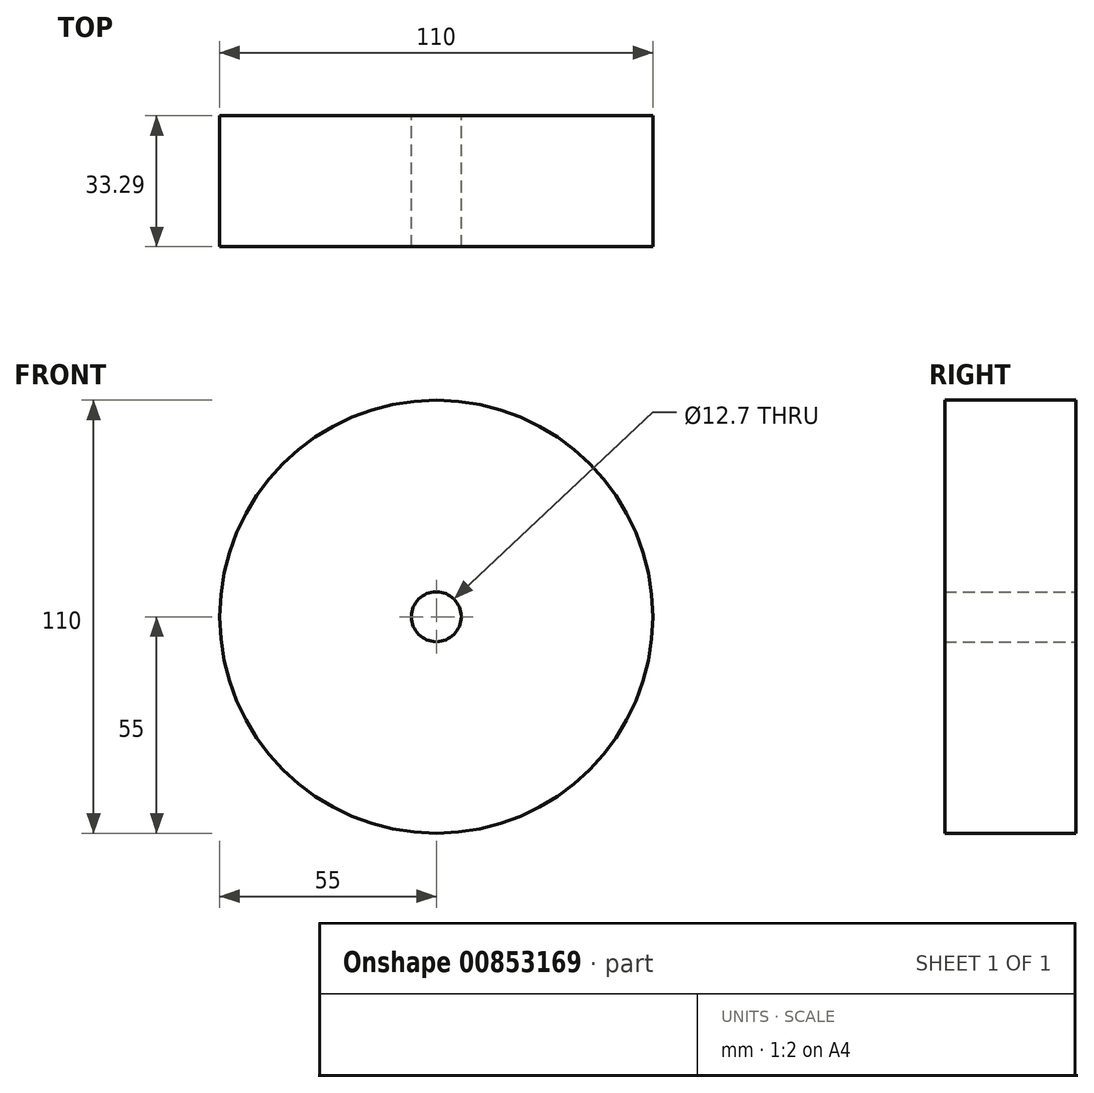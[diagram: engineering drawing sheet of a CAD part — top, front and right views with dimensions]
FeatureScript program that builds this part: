
annotation { "Feature Type Name" : "Feature", "Feature Type Description" : "" }
export const myFeature = defineFeature(function(context is Context, id is Id, definition is map)
    precondition{}
    {
        {
            var Q0;
            Q0=qCreatedBy(makeId("Front.planeOp"),FACE);
            var sketch = newSketch(context, id + "F0", { "sketchPlane" : qUnion([Q0])});
            skCircle(sketch, "E0", {"center": v(0, 0) * mm, "radius": 55 * mm});
            skSolve(sketch);
        }
        {
            var Q0;
            Q0=makeQuery(id+"F0.imprint","IMPRINT",FACE,{"disambiguationData":[TD([[makeQuery(id+"F0.imprint","IMPRINT",EDGE,{"derivedFrom":sQuery(id+"F0.wireOp",EDGE,"E0")}),1.0]])]});
            extrude(context, id + "F1", {"entities" : qUnion([Q0]), "depth" : 33.3 * mm, "offsetDistance" : 25.4 * mm});
        }
        {
            var Q0;
            Q0=qCreatedBy(makeId("Front.planeOp"),FACE);
            var sketch = newSketch(context, id + "F2", { "sketchPlane" : qUnion([Q0])});
            skPoint(sketch, "E1", {"position": v(0, 0) * mm});
            skSolve(sketch);
        }
        {
            var Q0;
            Q0=sQuery(id+"F2.wireOp",VERTEX,"E1");
            var Q1;
            Q1=makeQuery(id+"F1.opExtrude","SWEPT_BODY",BODY,{"disambiguationData":[OSD([sQuery(id+"F0.wireOp",EDGE,"E0")])]});
            hole(context, id + "F3", {"style" : HoleStyle.SIMPLE, "endStyle" : HoleEndStyle.THROUGH, "oppositeDirection" : true, "holeDiameter" : 12.7 * mm, "majorDiameter" : 6.35 * mm, "isTappedThrough" : true, "tappedDepth" : 12.7 * mm, "tapClearance" : 3, "locations" : qUnion([Q0]), "scope" : qUnion([Q1])});
        }
    });
